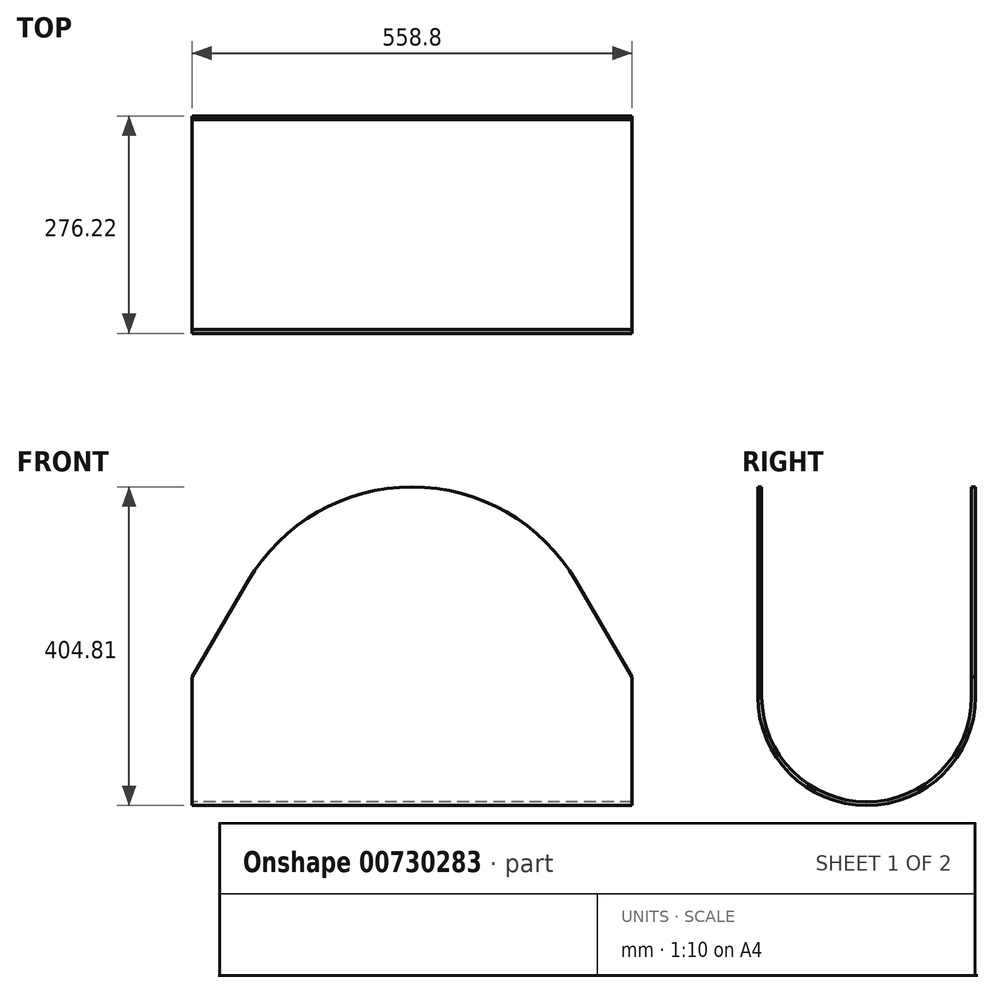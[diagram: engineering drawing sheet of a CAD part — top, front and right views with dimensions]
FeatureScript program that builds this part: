
annotation { "Feature Type Name" : "Feature", "Feature Type Description" : "" }
export const myFeature = defineFeature(function(context is Context, id is Id, definition is map)
    precondition{}
    {
        {
            var Q0;
            Q0=qCreatedBy(makeId("Right.planeOp"),FACE);
            var sketch = newSketch(context, id + "F0", { "sketchPlane" : qUnion([Q0])});
            skArc(sketch, "E0", {"start": v(133.35, 0) * mm, "mid": v(0, -133.35) * mm, "end": v(-133.35, 0) * mm});
            skLineSegment(sketch, "E1", {"start": v(-133.35, 0) * mm, "end": v(-133.35, 406.4) * mm});
            skLineSegment(sketch, "E2", {"start": v(133.35, 0) * mm, "end": v(133.35, 406.4) * mm});
            skLineSegment(sketch, "E3", {"start": v(-133.35, 0) * mm, "end": v(133.35, 0) * mm, "construction": true});
            skLineSegment(sketch, "E4.0", {"start": v(-138.11, 0) * mm, "end": v(-138.11, 406.4) * mm});
            skArc(sketch, "E4.1", {"start": v(138.11, 0) * mm, "mid": v(0, -138.11) * mm, "end": v(-138.11, 0) * mm});
            skLineSegment(sketch, "E4.2", {"start": v(138.11, 0) * mm, "end": v(138.11, 406.4) * mm});
            skLineSegment(sketch, "E5", {"start": v(-138.11, 406.4) * mm, "end": v(-133.35, 406.4) * mm});
            skLineSegment(sketch, "E6", {"start": v(138.11, 406.4) * mm, "end": v(133.35, 406.4) * mm});
            skSolve(sketch);
        }
        {
            var Q0;
            Q0=qSketchRegion(id+"F0",true);
            extrude(context, id + "F1", {"entities" : qUnion([Q0]), "endBound" : BoundingType.SYMMETRIC, "depth" : 558.8 * mm});
        }
        {
            var Q0;
            Q0=makeQuery(id+"F1.opExtrude","SWEPT_FACE",FACE,{"disambiguationData":[OSD([sQuery(id+"F0.wireOp",EDGE,"E4.2")])]});
            var sketch = newSketch(context, id + "F2", { "sketchPlane" : qUnion([Q0])});
            skArc(sketch, "E7", {"start": v(208.4, 147.04) * mm, "mid": v(0, 266.7) * mm, "end": v(-208.4, 147.04) * mm});
            skLineSegment(sketch, "E8", {"start": v(-208.4, 147.04) * mm, "end": v(-279.4, 25.4) * mm});
            skLineSegment(sketch, "E9", {"start": v(-279.4, 25.4) * mm, "end": v(-279.4, 406.4) * mm});
            skLineSegment(sketch, "E10", {"start": v(-279.4, 406.4) * mm, "end": v(279.4, 406.4) * mm});
            skLineSegment(sketch, "E11", {"start": v(279.4, 406.4) * mm, "end": v(279.4, 25.4) * mm});
            skLineSegment(sketch, "E12", {"start": v(208.4, 147.04) * mm, "end": v(279.4, 25.4) * mm});
            skSolve(sketch);
        }
        {
            var Q0;
            Q0=makeQuery(id+"F2.imprint","IMPRINT",FACE,{"disambiguationData":[TD([[makeQuery(id+"F2.imprint","IMPRINT",EDGE,{"derivedFrom":sQuery(id+"F2.wireOp",EDGE,"E7")}),-1.0]])]});
            extrude(context, id + "F3", {"entities" : qUnion([Q0]), "operationType" : NewBodyOperationType.REMOVE, "endBound" : BoundingType.THROUGH_ALL, "oppositeDirection" : true, "depth" : 25.4 * mm});
        }
    });
